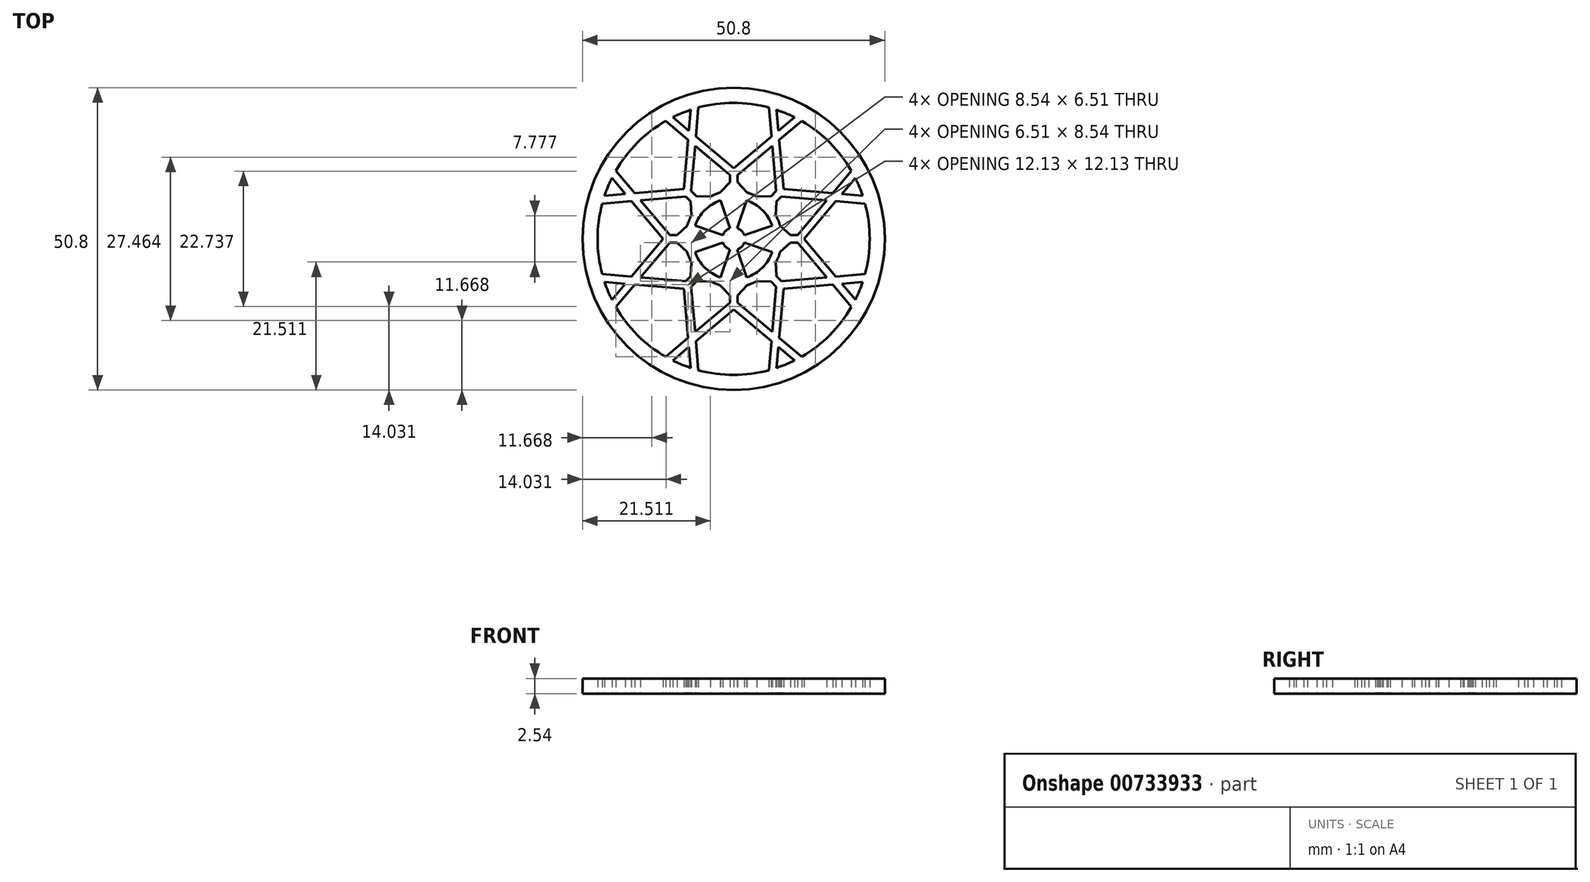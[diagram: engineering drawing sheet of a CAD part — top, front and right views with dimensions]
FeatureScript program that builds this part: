
annotation { "Feature Type Name" : "Feature", "Feature Type Description" : "" }
export const myFeature = defineFeature(function(context is Context, id is Id, definition is map)
    precondition{}
    {
        {
            var Q0;
            Q0=qCreatedBy(makeId("Top.planeOp"),FACE);
            var sketch = newSketch(context, id + "F0", { "sketchPlane" : qUnion([Q0])});
            skCircle(sketch, "E0", {"center": v(0, 0) * mm, "radius": 25.4 * mm});
            skArc(sketch, "E1.0", {"start": v(-11.43, 19.8) * mm, "mid": v(-16.16, 16.16) * mm, "end": v(-19.8, 11.43) * mm});
            skLineSegment(sketch, "E2", {"start": v(-0.61, 1.8) * mm, "end": v(-2.2, 6.47) * mm});
            skLineSegment(sketch, "E3", {"start": v(-0.63, 9.52) * mm, "end": v(-2.24, 7.8) * mm});
            skLineSegment(sketch, "E4", {"start": v(0.64, 9.52) * mm, "end": v(2.24, 7.8) * mm});
            skLineSegment(sketch, "E5", {"start": v(0.61, 1.8) * mm, "end": v(2.2, 6.47) * mm});
            skLineSegment(sketch, "E6.1.0", {"start": v(-6.28, 7.18) * mm, "end": v(-3.92, 7.1) * mm});
            skLineSegment(sketch, "E6.1.2", {"start": v(-7.18, 6.28) * mm, "end": v(-7.1, 3.92) * mm});
            skLineSegment(sketch, "E6.2.0", {"start": v(-9.52, 0.64) * mm, "end": v(-7.8, 2.24) * mm});
            skLineSegment(sketch, "E6.2.1", {"start": v(-1.8, 0.61) * mm, "end": v(-6.47, 2.2) * mm});
            skLineSegment(sketch, "E6.2.2", {"start": v(-9.52, -0.63) * mm, "end": v(-7.8, -2.24) * mm});
            skLineSegment(sketch, "E6.2.3", {"start": v(-1.8, -0.61) * mm, "end": v(-6.47, -2.2) * mm});
            skLineSegment(sketch, "E6.3.0", {"start": v(-7.18, -6.28) * mm, "end": v(-7.1, -3.92) * mm});
            skLineSegment(sketch, "E6.3.2", {"start": v(-6.28, -7.18) * mm, "end": v(-3.92, -7.1) * mm});
            skLineSegment(sketch, "E6.4.0", {"start": v(-0.64, -9.52) * mm, "end": v(-2.24, -7.8) * mm});
            skLineSegment(sketch, "E6.4.1", {"start": v(-0.61, -1.8) * mm, "end": v(-2.2, -6.47) * mm});
            skLineSegment(sketch, "E6.4.2", {"start": v(0.63, -9.52) * mm, "end": v(2.24, -7.8) * mm});
            skLineSegment(sketch, "E6.4.3", {"start": v(0.61, -1.8) * mm, "end": v(2.2, -6.47) * mm});
            skLineSegment(sketch, "E6.5.0", {"start": v(6.28, -7.18) * mm, "end": v(3.92, -7.1) * mm});
            skLineSegment(sketch, "E6.5.2", {"start": v(7.18, -6.28) * mm, "end": v(7.1, -3.92) * mm});
            skLineSegment(sketch, "E6.6.0", {"start": v(9.52, -0.64) * mm, "end": v(7.8, -2.24) * mm});
            skLineSegment(sketch, "E6.6.1", {"start": v(1.8, -0.61) * mm, "end": v(6.47, -2.2) * mm});
            skLineSegment(sketch, "E6.6.2", {"start": v(9.52, 0.63) * mm, "end": v(7.8, 2.24) * mm});
            skLineSegment(sketch, "E6.6.3", {"start": v(1.8, 0.61) * mm, "end": v(6.47, 2.2) * mm});
            skLineSegment(sketch, "E6.7.0", {"start": v(7.18, 6.28) * mm, "end": v(7.1, 3.92) * mm});
            skLineSegment(sketch, "E6.7.2", {"start": v(6.28, 7.18) * mm, "end": v(3.92, 7.1) * mm});
            skLineSegment(sketch, "E7", {"start": v(0.64, 10.74) * mm, "end": v(6.48, 15.64) * mm});
            skLineSegment(sketch, "E8", {"start": v(-0.63, 10.74) * mm, "end": v(-6.48, 15.64) * mm});
            skLineSegment(sketch, "E9.0", {"start": v(0, 11.86) * mm, "end": v(-6.34, 17.19) * mm});
            skLineSegment(sketch, "E10.0", {"start": v(0, 11.86) * mm, "end": v(6.34, 17.19) * mm});
            skPoint(sketch, "E11.orphan", {"position": v(0, 10.2) * mm});
            skLineSegment(sketch, "E12.trimOffspring", {"start": v(-0.63, 10.74) * mm, "end": v(-0.63, 9.52) * mm});
            skLineSegment(sketch, "E13.trimOffspring", {"start": v(0.64, 10.74) * mm, "end": v(0.64, 9.52) * mm});
            skArc(sketch, "E14.trimOffspring", {"start": v(10.23, 20.45) * mm, "mid": v(8.75, 21.12) * mm, "end": v(7.23, 21.69) * mm});
            skLineSegment(sketch, "E15.1.0", {"start": v(-7.14, 8.04) * mm, "end": v(-6.28, 7.18) * mm});
            skLineSegment(sketch, "E15.1.1", {"start": v(-8.04, 7.14) * mm, "end": v(-7.18, 6.28) * mm});
            skLineSegment(sketch, "E15.1.2", {"start": v(-8.04, 7.14) * mm, "end": v(-15.64, 6.48) * mm});
            skLineSegment(sketch, "E15.1.3", {"start": v(-8.39, 8.39) * mm, "end": v(-16.64, 7.67) * mm});
            skLineSegment(sketch, "E15.1.4", {"start": v(-8.39, 8.39) * mm, "end": v(-7.67, 16.64) * mm});
            skLineSegment(sketch, "E15.1.5", {"start": v(-7.14, 8.04) * mm, "end": v(-6.48, 15.64) * mm});
            skLineSegment(sketch, "E15.2.0", {"start": v(-10.74, 0.64) * mm, "end": v(-9.52, 0.64) * mm});
            skLineSegment(sketch, "E15.2.1", {"start": v(-10.74, -0.63) * mm, "end": v(-9.52, -0.63) * mm});
            skLineSegment(sketch, "E15.2.2", {"start": v(-10.74, -0.63) * mm, "end": v(-15.64, -6.48) * mm});
            skLineSegment(sketch, "E15.2.3", {"start": v(-11.86, 0) * mm, "end": v(-17.19, -6.34) * mm});
            skLineSegment(sketch, "E15.2.4", {"start": v(-11.86, 0) * mm, "end": v(-17.19, 6.34) * mm});
            skLineSegment(sketch, "E15.2.5", {"start": v(-10.74, 0.64) * mm, "end": v(-15.64, 6.48) * mm});
            skLineSegment(sketch, "E15.3.0", {"start": v(-8.04, -7.14) * mm, "end": v(-7.18, -6.28) * mm});
            skLineSegment(sketch, "E15.3.1", {"start": v(-7.14, -8.04) * mm, "end": v(-6.28, -7.18) * mm});
            skLineSegment(sketch, "E15.3.2", {"start": v(-7.14, -8.04) * mm, "end": v(-6.48, -15.64) * mm});
            skLineSegment(sketch, "E15.3.3", {"start": v(-8.39, -8.39) * mm, "end": v(-7.67, -16.64) * mm});
            skLineSegment(sketch, "E15.3.4", {"start": v(-8.39, -8.39) * mm, "end": v(-16.64, -7.67) * mm});
            skLineSegment(sketch, "E15.3.5", {"start": v(-8.04, -7.14) * mm, "end": v(-15.64, -6.48) * mm});
            skLineSegment(sketch, "E15.4.0", {"start": v(-0.64, -10.74) * mm, "end": v(-0.64, -9.52) * mm});
            skLineSegment(sketch, "E15.4.1", {"start": v(0.63, -10.74) * mm, "end": v(0.63, -9.52) * mm});
            skLineSegment(sketch, "E15.4.2", {"start": v(0.63, -10.74) * mm, "end": v(6.48, -15.64) * mm});
            skLineSegment(sketch, "E15.4.3", {"start": v(0, -11.86) * mm, "end": v(6.34, -17.19) * mm});
            skLineSegment(sketch, "E15.4.4", {"start": v(0, -11.86) * mm, "end": v(-6.34, -17.19) * mm});
            skLineSegment(sketch, "E15.4.5", {"start": v(-0.64, -10.74) * mm, "end": v(-6.48, -15.64) * mm});
            skLineSegment(sketch, "E15.5.0", {"start": v(7.14, -8.04) * mm, "end": v(6.28, -7.18) * mm});
            skLineSegment(sketch, "E15.5.1", {"start": v(8.04, -7.14) * mm, "end": v(7.18, -6.28) * mm});
            skLineSegment(sketch, "E15.5.2", {"start": v(8.04, -7.14) * mm, "end": v(15.64, -6.48) * mm});
            skLineSegment(sketch, "E15.5.3", {"start": v(8.39, -8.39) * mm, "end": v(16.64, -7.67) * mm});
            skLineSegment(sketch, "E15.5.4", {"start": v(8.39, -8.39) * mm, "end": v(7.67, -16.64) * mm});
            skLineSegment(sketch, "E15.5.5", {"start": v(7.14, -8.04) * mm, "end": v(6.48, -15.64) * mm});
            skLineSegment(sketch, "E15.6.0", {"start": v(10.74, -0.64) * mm, "end": v(9.52, -0.64) * mm});
            skLineSegment(sketch, "E15.6.1", {"start": v(10.74, 0.63) * mm, "end": v(9.52, 0.63) * mm});
            skLineSegment(sketch, "E15.6.2", {"start": v(10.74, 0.63) * mm, "end": v(15.64, 6.48) * mm});
            skLineSegment(sketch, "E15.6.3", {"start": v(11.86, 0) * mm, "end": v(17.19, 6.34) * mm});
            skLineSegment(sketch, "E15.6.4", {"start": v(11.86, 0) * mm, "end": v(17.19, -6.34) * mm});
            skLineSegment(sketch, "E15.6.5", {"start": v(10.74, -0.64) * mm, "end": v(15.64, -6.48) * mm});
            skLineSegment(sketch, "E15.7.0", {"start": v(8.04, 7.14) * mm, "end": v(7.18, 6.28) * mm});
            skLineSegment(sketch, "E15.7.1", {"start": v(7.14, 8.04) * mm, "end": v(6.28, 7.18) * mm});
            skLineSegment(sketch, "E15.7.2", {"start": v(7.14, 8.04) * mm, "end": v(6.48, 15.64) * mm});
            skLineSegment(sketch, "E15.7.3", {"start": v(8.39, 8.39) * mm, "end": v(7.67, 16.64) * mm});
            skLineSegment(sketch, "E15.7.4", {"start": v(8.39, 8.39) * mm, "end": v(16.64, 7.67) * mm});
            skLineSegment(sketch, "E15.7.5", {"start": v(8.04, 7.14) * mm, "end": v(15.64, 6.48) * mm});
            skPoint(sketch, "E16.orphan", {"position": v(-7.21, 7.21) * mm});
            skPoint(sketch, "E17.orphan", {"position": v(-10.2, 0) * mm});
            skPoint(sketch, "E18.orphan", {"position": v(-7.21, -7.21) * mm});
            skPoint(sketch, "E19.orphan", {"position": v(0, -10.2) * mm});
            skPoint(sketch, "E20.orphan", {"position": v(7.21, -7.21) * mm});
            skPoint(sketch, "E21.orphan", {"position": v(10.2, 0) * mm});
            skPoint(sketch, "E22.orphan", {"position": v(7.21, 7.21) * mm});
            skLineSegment(sketch, "E23.trimOffspring", {"start": v(-18.18, 7.53) * mm, "end": v(-21.69, 7.23) * mm});
            skLineSegment(sketch, "E24.trimOffspring", {"start": v(-18.18, 7.53) * mm, "end": v(-20.45, 10.23) * mm});
            skLineSegment(sketch, "E25.trimOffspring", {"start": v(-17.19, 6.34) * mm, "end": v(-22.08, 5.92) * mm});
            skLineSegment(sketch, "E26.trimOffspring", {"start": v(-16.64, 7.67) * mm, "end": v(-19.8, 11.43) * mm});
            skLineSegment(sketch, "E27.trimOffspring", {"start": v(-7.53, 18.18) * mm, "end": v(-10.23, 20.45) * mm});
            skLineSegment(sketch, "E28.trimOffspring", {"start": v(-7.53, 18.18) * mm, "end": v(-7.23, 21.69) * mm});
            skLineSegment(sketch, "E29.trimOffspring", {"start": v(-7.67, 16.64) * mm, "end": v(-11.43, 19.8) * mm});
            skPoint(sketch, "E30.orphan", {"position": v(-5.92, 22.08) * mm});
            skLineSegment(sketch, "E31.trimOffspring", {"start": v(-17.19, -6.34) * mm, "end": v(-22.08, -5.92) * mm});
            skLineSegment(sketch, "E32.trimOffspring", {"start": v(-16.64, -7.67) * mm, "end": v(-19.8, -11.43) * mm});
            skLineSegment(sketch, "E33.trimOffspring", {"start": v(-18.18, -7.53) * mm, "end": v(-21.69, -7.23) * mm});
            skLineSegment(sketch, "E34.trimOffspring", {"start": v(-18.18, -7.53) * mm, "end": v(-20.45, -10.23) * mm});
            skArc(sketch, "E35.trimOffspring", {"start": v(-19.8, -11.43) * mm, "mid": v(-16.16, -16.16) * mm, "end": v(-11.43, -19.8) * mm});
            skArc(sketch, "E36.trimOffspring", {"start": v(-21.69, -7.23) * mm, "mid": v(-21.12, -8.75) * mm, "end": v(-20.45, -10.23) * mm});
            skLineSegment(sketch, "E37.trimOffspring", {"start": v(-6.34, 17.19) * mm, "end": v(-5.92, 22.08) * mm});
            skArc(sketch, "E38.trimOffspring", {"start": v(-7.23, 21.69) * mm, "mid": v(-8.75, 21.12) * mm, "end": v(-10.23, 20.45) * mm});
            skArc(sketch, "E39.trimOffspring", {"start": v(5.92, 22.08) * mm, "mid": v(0, 22.86) * mm, "end": v(-5.92, 22.08) * mm});
            skLineSegment(sketch, "E40.trimOffspring", {"start": v(7.53, 18.18) * mm, "end": v(10.23, 20.45) * mm});
            skLineSegment(sketch, "E41.trimOffspring", {"start": v(7.53, 18.18) * mm, "end": v(7.23, 21.69) * mm});
            skLineSegment(sketch, "E42.trimOffspring", {"start": v(7.67, 16.64) * mm, "end": v(11.43, 19.8) * mm});
            skLineSegment(sketch, "E43.trimOffspring", {"start": v(6.34, 17.19) * mm, "end": v(5.92, 22.08) * mm});
            skArc(sketch, "E44.trimOffspring", {"start": v(19.8, 11.43) * mm, "mid": v(16.16, 16.16) * mm, "end": v(11.43, 19.8) * mm});
            skArc(sketch, "E45.trimOffspring", {"start": v(21.69, 7.23) * mm, "mid": v(21.12, 8.75) * mm, "end": v(20.45, 10.23) * mm});
            skLineSegment(sketch, "E46.trimOffspring", {"start": v(18.18, 7.53) * mm, "end": v(21.69, 7.23) * mm});
            skLineSegment(sketch, "E47.trimOffspring", {"start": v(17.19, 6.34) * mm, "end": v(22.08, 5.92) * mm});
            skLineSegment(sketch, "E48.trimOffspring", {"start": v(16.64, 7.67) * mm, "end": v(19.8, 11.43) * mm});
            skLineSegment(sketch, "E49.trimOffspring", {"start": v(18.18, 7.53) * mm, "end": v(20.45, 10.23) * mm});
            skArc(sketch, "E50.trimOffspring", {"start": v(20.45, -10.23) * mm, "mid": v(21.12, -8.75) * mm, "end": v(21.69, -7.23) * mm});
            skArc(sketch, "E51.trimOffspring", {"start": v(22.08, -5.92) * mm, "mid": v(22.86, 0) * mm, "end": v(22.08, 5.92) * mm});
            skLineSegment(sketch, "E52.trimOffspring", {"start": v(17.19, -6.34) * mm, "end": v(22.08, -5.92) * mm});
            skLineSegment(sketch, "E53.trimOffspring", {"start": v(16.64, -7.67) * mm, "end": v(19.8, -11.43) * mm});
            skLineSegment(sketch, "E54.trimOffspring", {"start": v(18.18, -7.53) * mm, "end": v(20.45, -10.23) * mm});
            skLineSegment(sketch, "E55.trimOffspring", {"start": v(18.18, -7.53) * mm, "end": v(21.69, -7.23) * mm});
            skArc(sketch, "E56.trimOffspring", {"start": v(7.23, -21.69) * mm, "mid": v(8.75, -21.12) * mm, "end": v(10.23, -20.45) * mm});
            skArc(sketch, "E57.trimOffspring", {"start": v(11.43, -19.8) * mm, "mid": v(16.16, -16.16) * mm, "end": v(19.8, -11.43) * mm});
            skLineSegment(sketch, "E58.trimOffspring", {"start": v(6.34, -17.19) * mm, "end": v(5.92, -22.08) * mm});
            skLineSegment(sketch, "E59.trimOffspring", {"start": v(7.67, -16.64) * mm, "end": v(11.43, -19.8) * mm});
            skLineSegment(sketch, "E60.trimOffspring", {"start": v(7.53, -18.18) * mm, "end": v(7.23, -21.69) * mm});
            skLineSegment(sketch, "E61.trimOffspring", {"start": v(7.53, -18.18) * mm, "end": v(10.23, -20.45) * mm});
            skArc(sketch, "E62.trimOffspring", {"start": v(-10.23, -20.45) * mm, "mid": v(-8.75, -21.12) * mm, "end": v(-7.23, -21.69) * mm});
            skArc(sketch, "E63.trimOffspring", {"start": v(-5.92, -22.08) * mm, "mid": v(0, -22.86) * mm, "end": v(5.92, -22.08) * mm});
            skLineSegment(sketch, "E64.trimOffspring", {"start": v(-7.67, -16.64) * mm, "end": v(-11.43, -19.8) * mm});
            skLineSegment(sketch, "E65.trimOffspring", {"start": v(-6.34, -17.19) * mm, "end": v(-5.92, -22.08) * mm});
            skLineSegment(sketch, "E66.trimOffspring", {"start": v(-7.53, -18.18) * mm, "end": v(-10.23, -20.45) * mm});
            skLineSegment(sketch, "E67.trimOffspring", {"start": v(-7.53, -18.18) * mm, "end": v(-7.23, -21.69) * mm});
            skArc(sketch, "E68.trimOffspring", {"start": v(-22.08, 5.92) * mm, "mid": v(-22.86, 0) * mm, "end": v(-22.08, -5.92) * mm});
            skArc(sketch, "E69.trimOffspring", {"start": v(-20.45, 10.23) * mm, "mid": v(-21.12, 8.75) * mm, "end": v(-21.69, 7.23) * mm});
            skArc(sketch, "E70", {"start": v(-6.47, -2.2) * mm, "mid": v(-4.84, -4.84) * mm, "end": v(-2.2, -6.47) * mm});
            skArc(sketch, "E71", {"start": v(-7.8, -2.24) * mm, "mid": v(-7.5, -3.1) * mm, "end": v(-7.1, -3.92) * mm});
            skPoint(sketch, "E72.orphan", {"position": v(-7.47, 2.54) * mm});
            skPoint(sketch, "E73.orphan", {"position": v(-7.47, -2.54) * mm});
            skPoint(sketch, "E74.orphan", {"position": v(-7.08, 3.49) * mm});
            skPoint(sketch, "E75.orphan", {"position": v(-3.49, 7.08) * mm});
            skArc(sketch, "E76.trimOffspring", {"start": v(-7.1, 3.92) * mm, "mid": v(-7.5, 3.1) * mm, "end": v(-7.8, 2.24) * mm});
            skArc(sketch, "E77.trimOffspring", {"start": v(-2.2, 6.47) * mm, "mid": v(-4.84, 4.84) * mm, "end": v(-6.47, 2.2) * mm});
            skArc(sketch, "E78.trimOffspring", {"start": v(-2.24, 7.8) * mm, "mid": v(-3.1, 7.5) * mm, "end": v(-3.92, 7.1) * mm});
            skPoint(sketch, "E79.orphan", {"position": v(-2.54, 7.47) * mm});
            skPoint(sketch, "E80.orphan", {"position": v(2.54, 7.47) * mm});
            skArc(sketch, "E81.trimOffspring", {"start": v(3.92, 7.1) * mm, "mid": v(3.1, 7.5) * mm, "end": v(2.24, 7.8) * mm});
            skPoint(sketch, "E82.orphan", {"position": v(3.49, 7.08) * mm});
            skPoint(sketch, "E83.orphan", {"position": v(7.08, 3.49) * mm});
            skArc(sketch, "E84.trimOffspring", {"start": v(6.47, 2.2) * mm, "mid": v(4.84, 4.84) * mm, "end": v(2.2, 6.47) * mm});
            skArc(sketch, "E85.trimOffspring", {"start": v(7.8, 2.24) * mm, "mid": v(7.5, 3.1) * mm, "end": v(7.1, 3.92) * mm});
            skPoint(sketch, "E86.orphan", {"position": v(7.47, 2.54) * mm});
            skPoint(sketch, "E87.orphan", {"position": v(7.47, -2.54) * mm});
            skArc(sketch, "E88.trimOffspring", {"start": v(7.1, -3.92) * mm, "mid": v(7.5, -3.1) * mm, "end": v(7.8, -2.24) * mm});
            skPoint(sketch, "E89.orphan", {"position": v(3.49, -7.08) * mm});
            skPoint(sketch, "E90.orphan", {"position": v(7.08, -3.49) * mm});
            skArc(sketch, "E91.trimOffspring", {"start": v(2.2, -6.47) * mm, "mid": v(4.84, -4.84) * mm, "end": v(6.47, -2.2) * mm});
            skArc(sketch, "E92.trimOffspring", {"start": v(2.24, -7.8) * mm, "mid": v(3.1, -7.5) * mm, "end": v(3.92, -7.1) * mm});
            skPoint(sketch, "E93.orphan", {"position": v(-2.54, -7.47) * mm});
            skPoint(sketch, "E94.orphan", {"position": v(2.54, -7.47) * mm});
            skArc(sketch, "E95.trimOffspring", {"start": v(-3.92, -7.1) * mm, "mid": v(-3.1, -7.5) * mm, "end": v(-2.24, -7.8) * mm});
            skPoint(sketch, "E96.orphan", {"position": v(-7.08, -3.49) * mm});
            skPoint(sketch, "E97.orphan", {"position": v(-3.49, -7.08) * mm});
            skArc(sketch, "E98", {"start": v(-0.61, 1.8) * mm, "mid": v(-1.35, 1.35) * mm, "end": v(-1.8, 0.61) * mm});
            skArc(sketch, "E99.trimOffspring", {"start": v(-1.8, -0.61) * mm, "mid": v(-1.35, -1.35) * mm, "end": v(-0.61, -1.8) * mm});
            skArc(sketch, "E100.trimOffspring", {"start": v(0.61, -1.8) * mm, "mid": v(1.35, -1.35) * mm, "end": v(1.8, -0.61) * mm});
            skArc(sketch, "E101.trimOffspring", {"start": v(1.8, 0.61) * mm, "mid": v(1.35, 1.35) * mm, "end": v(0.61, 1.8) * mm});
            skSolve(sketch);
        }
        {
            var Q0;
            Q0=makeQuery(id+"F0.imprint","IMPRINT",FACE,{"disambiguationData":[TD([[makeQuery(id+"F0.imprint","IMPRINT",EDGE,{"derivedFrom":sQuery(id+"F0.wireOp",EDGE,"E0")}),1.0]])]});
            extrude(context, id + "F1", {"entities" : qUnion([Q0]), "depth" : 2.54 * mm, "offsetDistance" : 25.4 * mm});
        }
    });
